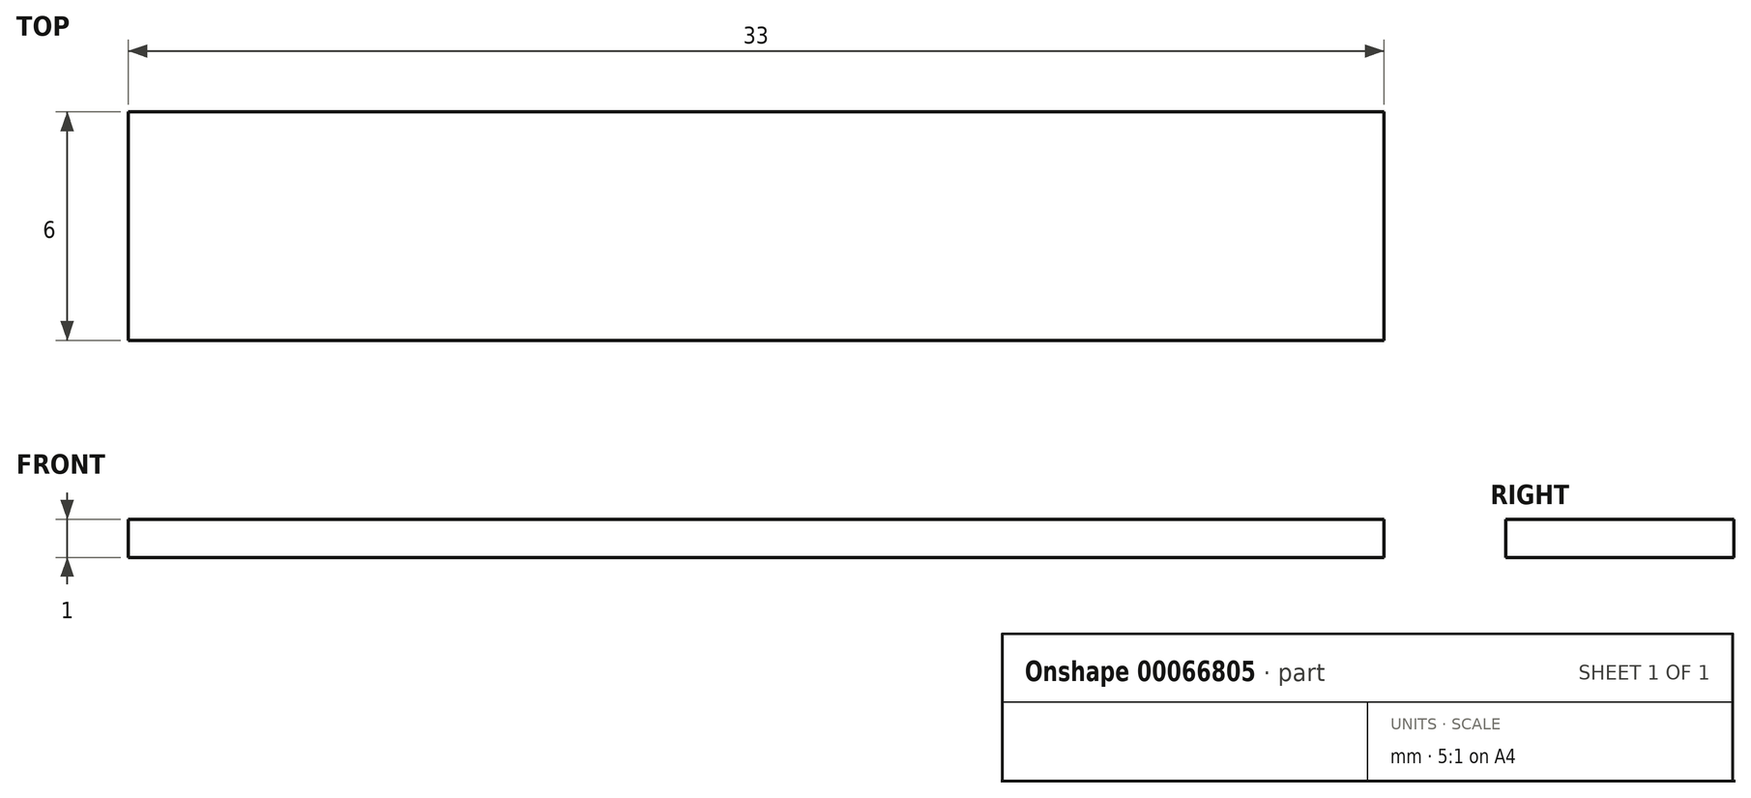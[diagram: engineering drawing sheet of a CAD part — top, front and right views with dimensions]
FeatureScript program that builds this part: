
annotation { "Feature Type Name" : "Feature", "Feature Type Description" : "" }
export const myFeature = defineFeature(function(context is Context, id is Id, definition is map)
    precondition{}
    {
        {
            var Q0;
            Q0=qCreatedBy(makeId("Top.planeOp"),FACE);
            var sketch = newSketch(context, id + "F0", { "sketchPlane" : qUnion([Q0])});
            skLineSegment(sketch, "E0.bottom", {"start": v(0, 0) * mm, "end": v(-33, 0) * mm});
            skLineSegment(sketch, "E0.top", {"start": v(0, 6) * mm, "end": v(-33, 6) * mm});
            skLineSegment(sketch, "E0.left", {"start": v(0, 0) * mm, "end": v(0, 6) * mm});
            skLineSegment(sketch, "E0.right", {"start": v(-33, 0) * mm, "end": v(-33, 6) * mm});
            skSolve(sketch);
        }
        {
            var Q0;
            Q0=makeQuery(id+"F0.imprint","IMPRINT",FACE,{"disambiguationData":[TD([[makeQuery(id+"F0.imprint","IMPRINT",EDGE,{"derivedFrom":sQuery(id+"F0.wireOp",EDGE,"E0.bottom")}),-1.0]])]});
            extrude(context, id + "F1", {"entities" : qUnion([Q0]), "depth" : 1 * mm});
        }
    });
